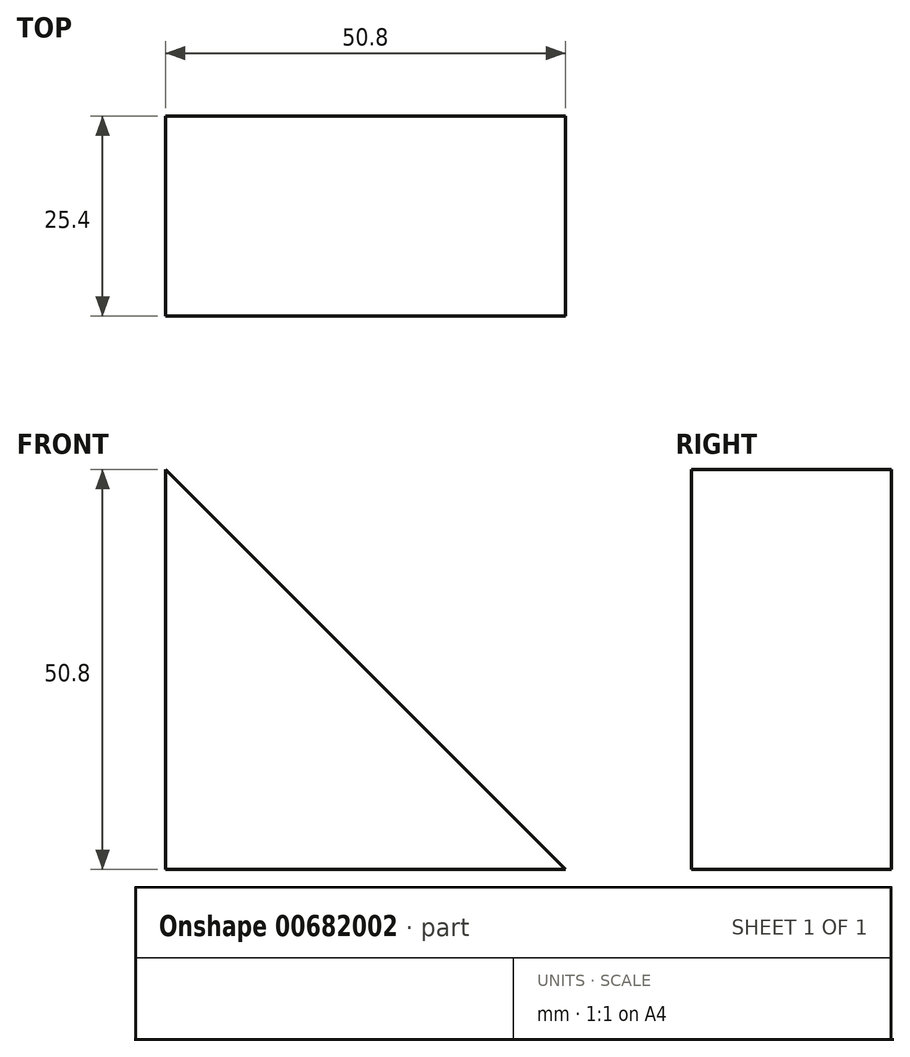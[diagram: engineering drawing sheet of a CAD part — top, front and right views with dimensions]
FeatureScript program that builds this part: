
annotation { "Feature Type Name" : "Feature", "Feature Type Description" : "" }
export const myFeature = defineFeature(function(context is Context, id is Id, definition is map)
    precondition{}
    {
        {
            var Q0;
            Q0=qCreatedBy(makeId("Front.planeOp"),FACE);
            var sketch = newSketch(context, id + "F0", { "sketchPlane" : qUnion([Q0])});
            skLineSegment(sketch, "E0", {"start": v(0, 0) * mm, "end": v(-50.8, 0) * mm});
            skLineSegment(sketch, "E1", {"start": v(-50.8, 0) * mm, "end": v(-50.8, 50.8) * mm});
            skLineSegment(sketch, "E2", {"start": v(-50.8, 50.8) * mm, "end": v(0, 0) * mm});
            skSolve(sketch);
        }
        {
            var Q0;
            Q0=makeQuery(id+"F0.imprint","IMPRINT",FACE,{"disambiguationData":[TD([[makeQuery(id+"F0.imprint","IMPRINT",EDGE,{"derivedFrom":sQuery(id+"F0.wireOp",EDGE,"E0")}),-1.0]])]});
            extrude(context, id + "F1", {"entities" : qUnion([Q0]), "depth" : 25.4 * mm, "offsetDistance" : 25.4 * mm});
        }
    });
